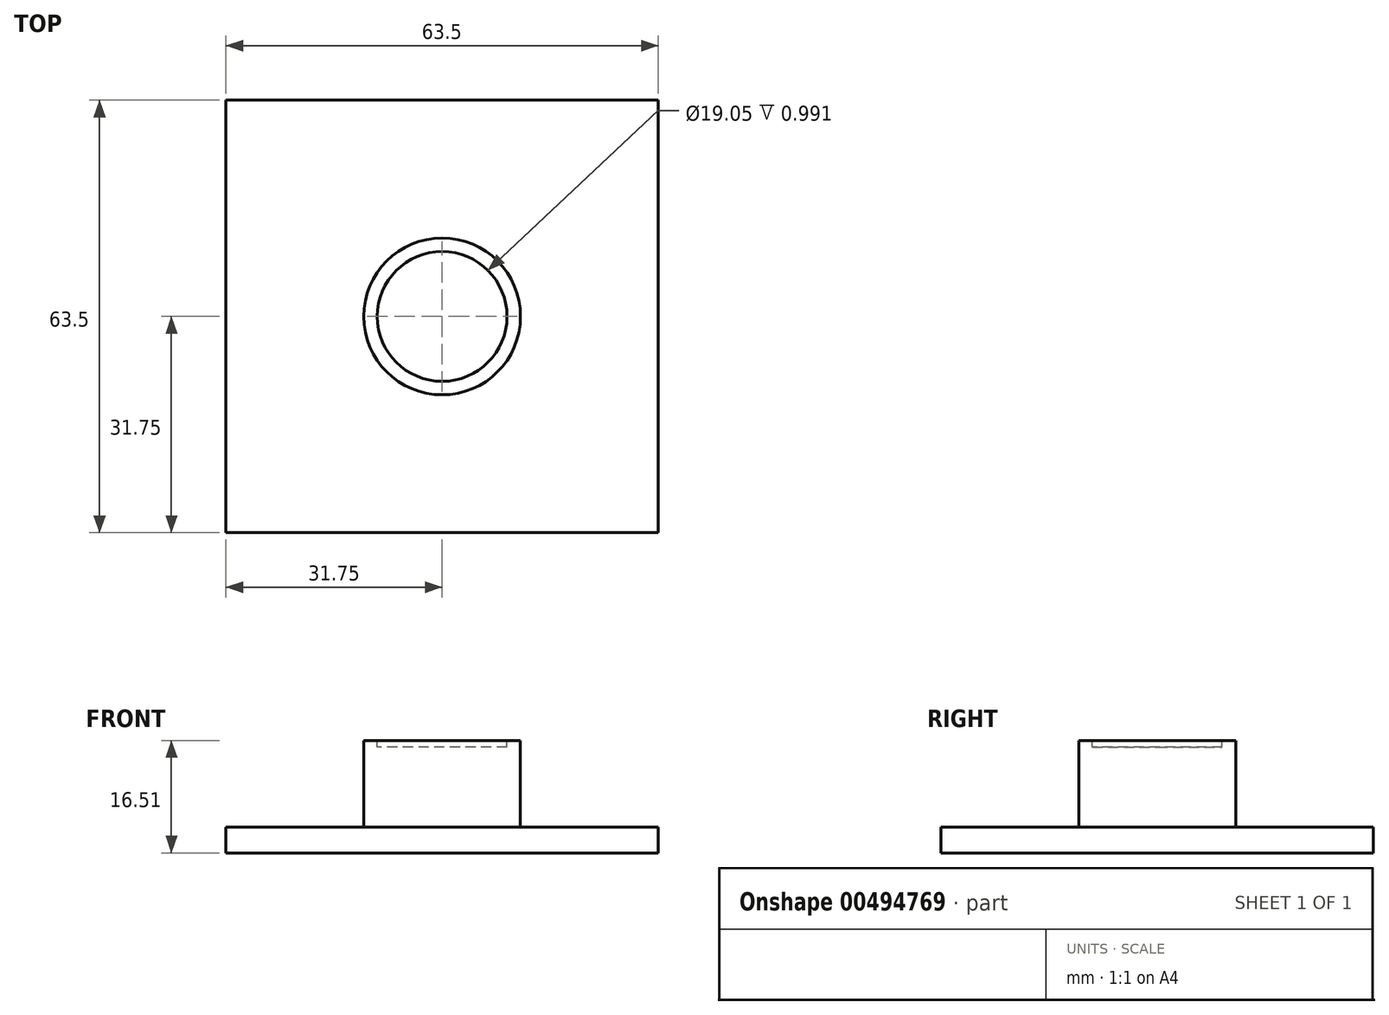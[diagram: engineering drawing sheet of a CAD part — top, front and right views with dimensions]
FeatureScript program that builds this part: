
annotation { "Feature Type Name" : "Feature", "Feature Type Description" : "" }
export const myFeature = defineFeature(function(context is Context, id is Id, definition is map)
    precondition{}
    {
        {
            var Q0;
            Q0=qCreatedBy(makeId("Top.planeOp"),FACE);
            var sketch = newSketch(context, id + "F0", { "sketchPlane" : qUnion([Q0])});
            skLineSegment(sketch, "E0.bottom", {"start": v(31.75, -31.75) * mm, "end": v(-31.75, -31.75) * mm});
            skLineSegment(sketch, "E0.top", {"start": v(31.75, 31.75) * mm, "end": v(-31.75, 31.75) * mm});
            skLineSegment(sketch, "E0.left", {"start": v(31.75, -31.75) * mm, "end": v(31.75, 31.75) * mm});
            skLineSegment(sketch, "E0.right", {"start": v(-31.75, -31.75) * mm, "end": v(-31.75, 31.75) * mm});
            skPoint(sketch, "E0.middle", {"position": v(0, 0) * mm});
            skSolve(sketch);
        }
        {
            var Q0;
            Q0 = qSketchRegion(id + "F0", true);
            extrude(context, id + "F1", {"entities" : qUnion([Q0]), "depth" : 3.8 * mm, "offsetDistance" : 25.4 * mm});
        }
        {
            var Q0;
            Q0=makeQuery(id+"F1.opExtrude","CAP_FACE",FACE,{"disambiguationData":[OSD([sQuery(id+"F0.wireOp",EDGE,"E0.bottom"),sQuery(id+"F0.wireOp",EDGE,"E0.top"),sQuery(id+"F0.wireOp",EDGE,"E0.left"),sQuery(id+"F0.wireOp",EDGE,"E0.right")])],"isStart":false});
            var sketch = newSketch(context, id + "F2", { "sketchPlane" : qUnion([Q0])});
            skCircle(sketch, "E1", {"center": v(0, 0) * mm, "radius": 11.5 * mm});
            skSolve(sketch);
        }
        {
            var Q0;
            Q0 = qSketchRegion(id + "F2", true);
            extrude(context, id + "F3", {"entities" : qUnion([Q0]), "operationType" : NewBodyOperationType.ADD, "depth" : 12.7 * mm, "offsetDistance" : 25.4 * mm});
        }
        {
            var Q0;
            Q0=makeQuery(id+"F3.opExtrude","CAP_FACE",FACE,{"disambiguationData":[OSD([sQuery(id+"F2.wireOp",EDGE,"E1")])],"isStart":false});
            var sketch = newSketch(context, id + "F4", { "sketchPlane" : qUnion([Q0])});
            skCircle(sketch, "E2", {"center": v(0, 0) * mm, "radius": 9.53 * mm});
            skSolve(sketch);
        }
        {
            var Q0;
            Q0 = qSketchRegion(id + "F4", true);
            extrude(context, id + "F5", {"entities" : qUnion([Q0]), "operationType" : NewBodyOperationType.REMOVE, "oppositeDirection" : true, "depth" : 1 * mm, "offsetDistance" : 25.4 * mm});
        }
    });
